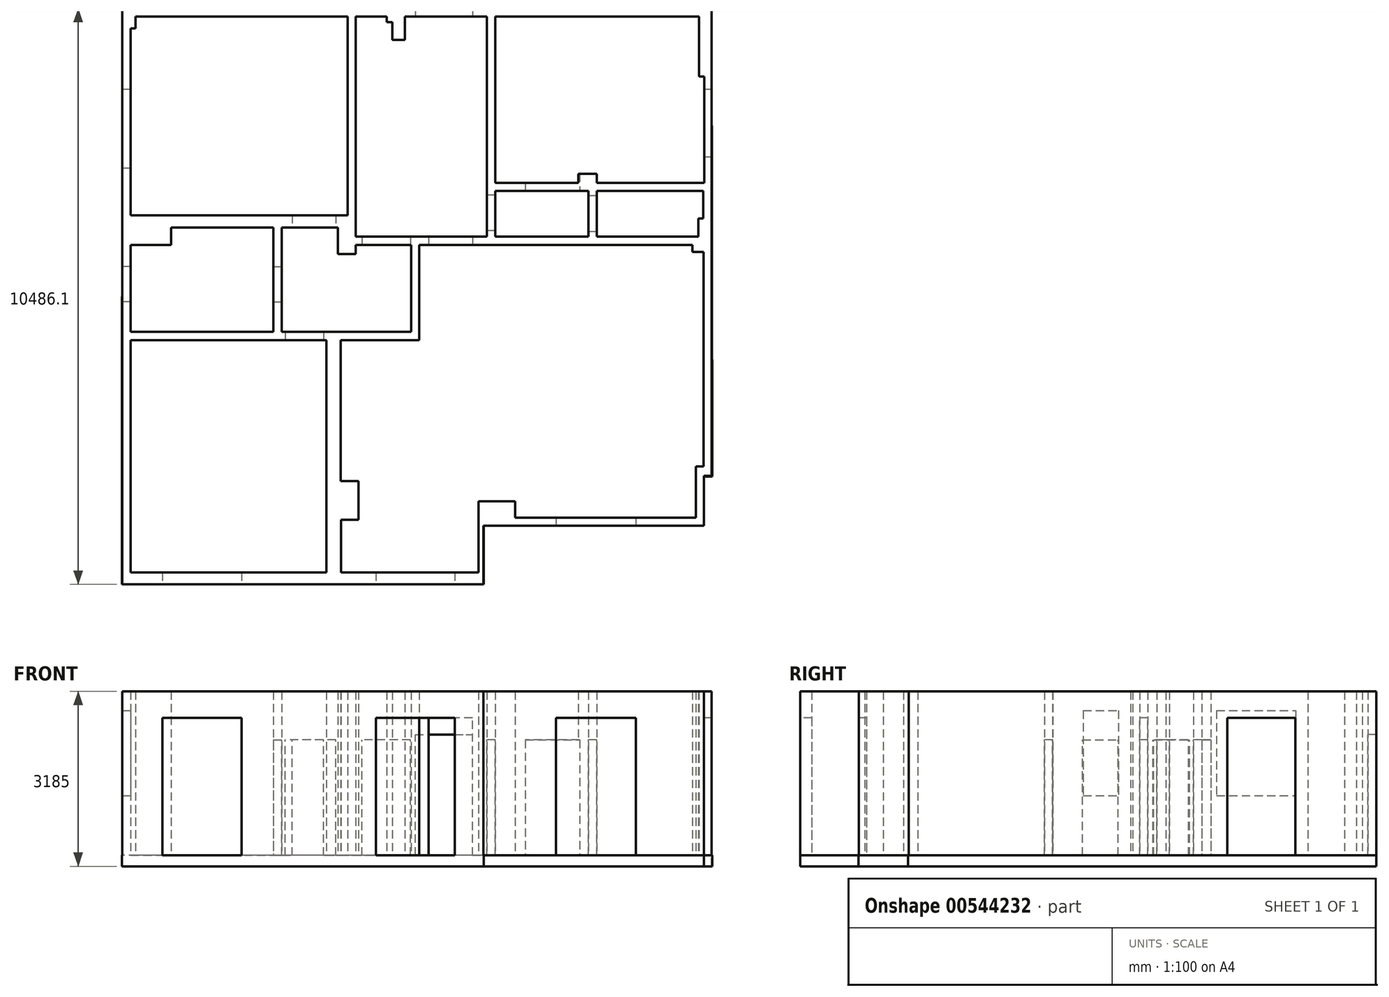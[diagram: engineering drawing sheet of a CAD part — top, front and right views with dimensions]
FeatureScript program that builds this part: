
annotation { "Feature Type Name" : "Feature", "Feature Type Description" : "" }
export const myFeature = defineFeature(function(context is Context, id is Id, definition is map)
    precondition{}
    {
        {
            var Q0;
            Q0=qCreatedBy(makeId("Top.planeOp"),FACE);
            var sketch = newSketch(context, id + "F0", { "sketchPlane" : qUnion([Q0])});
            skLineSegment(sketch, "E0", {"start": v(0, 0) * mm, "end": v(4001, 0) * mm});
            skLineSegment(sketch, "E1", {"start": v(4001, 0) * mm, "end": v(4001, -125) * mm});
            skLineSegment(sketch, "E2", {"start": v(4001, -125) * mm, "end": v(4202.95, -125) * mm});
            skLineSegment(sketch, "E3", {"start": v(4202.95, -125) * mm, "end": v(4202.95, -4036) * mm});
            skLineSegment(sketch, "E4", {"start": v(4202.95, -4036) * mm, "end": v(4062.95, -4036) * mm});
            skLineSegment(sketch, "E5", {"start": v(4062.95, -4036) * mm, "end": v(4062.95, -4967) * mm});
            skLineSegment(sketch, "E6", {"start": v(4062.95, -4967) * mm, "end": v(2970.95, -4967) * mm});
            skLineSegment(sketch, "E7", {"start": v(2970.95, -4967) * mm, "end": v(1520.95, -4967) * mm});
            skLineSegment(sketch, "E8", {"start": v(1520.95, -4967) * mm, "end": v(778.95, -4967) * mm});
            skLineSegment(sketch, "E9", {"start": v(-797, 0) * mm, "end": v(0, 0) * mm});
            skLineSegment(sketch, "E10", {"start": v(778.95, -4967) * mm, "end": v(778.95, -4667) * mm});
            skLineSegment(sketch, "E11", {"start": v(778.95, -4667) * mm, "end": v(106.95, -4667) * mm});
            skLineSegment(sketch, "E12", {"start": v(106.95, -4667) * mm, "end": v(106.95, -5966) * mm});
            skLineSegment(sketch, "E13", {"start": v(106.95, -5966) * mm, "end": v(-320.05, -5966) * mm});
            skLineSegment(sketch, "E14", {"start": v(-320.05, -5966) * mm, "end": v(-1760.05, -5966) * mm});
            skLineSegment(sketch, "E15", {"start": v(-1760.05, -5966) * mm, "end": v(-2394.05, -5966) * mm});
            skLineSegment(sketch, "E16", {"start": v(-2394.05, -5966) * mm, "end": v(-2394.05, -5002) * mm});
            skLineSegment(sketch, "E17", {"start": v(-2394.05, -5002) * mm, "end": v(-2075.05, -5002) * mm});
            skLineSegment(sketch, "E18", {"start": v(-2075.05, -5002) * mm, "end": v(-2075.05, -4297) * mm});
            skLineSegment(sketch, "E19", {"start": v(-2075.05, -4297) * mm, "end": v(-2399.05, -4297) * mm});
            skLineSegment(sketch, "E20", {"start": v(-2399.05, -4297) * mm, "end": v(-2399.05, -1733) * mm});
            skLineSegment(sketch, "E21", {"start": v(-797, 0) * mm, "end": v(-967, 0) * mm});
            skLineSegment(sketch, "E22", {"start": v(-967, 0) * mm, "end": v(-967, -1733) * mm});
            skLineSegment(sketch, "E23", {"start": v(-2399.05, -1733) * mm, "end": v(-967, -1733) * mm});
            skLineSegment(sketch, "E24.1", {"start": v(-797, -5.1) * mm, "end": v(-961.9, -5.1) * mm});
            skLineSegment(sketch, "E24.5", {"start": v(-2181.9, -4291.9) * mm, "end": v(-2505.9, -4291.9) * mm});
            skLineSegment(sketch, "E24.11", {"start": v(-797, -5.1) * mm, "end": v(0, -5.1) * mm});
            skLineSegment(sketch, "E24.19", {"start": v(3945.9, -4961.9) * mm, "end": v(2859, -4961.9) * mm});
            skLineSegment(sketch, "E25.0", {"start": v(0, 150) * mm, "end": v(264.38, 150) * mm});
            skLineSegment(sketch, "E26.0", {"start": v(2800.47, -5111.9) * mm, "end": v(1350.47, -5111.9) * mm});
            skLineSegment(sketch, "E27.0", {"start": v(1409, -5111.9) * mm, "end": v(720.85, -5111.9) * mm});
            skLineSegment(sketch, "E28", {"start": v(720.85, -5111.9) * mm, "end": v(198.85, -5111.9) * mm});
            skLineSegment(sketch, "E29", {"start": v(198.85, -5111.9) * mm, "end": v(198.85, -6179.3) * mm});
            skLineSegment(sketch, "E30", {"start": v(-435.2, -6179.3) * mm, "end": v(198.85, -6179.3) * mm});
            skLineSegment(sketch, "E31", {"start": v(2800.47, -5111.9) * mm, "end": v(4212.95, -5111.9) * mm});
            skLineSegment(sketch, "E32", {"start": v(-435.2, -6179.3) * mm, "end": v(-1872, -6179.3) * mm});
            skLineSegment(sketch, "E33", {"start": v(-1872, -6179.3) * mm, "end": v(-2660.9, -6179.3) * mm});
            skLineSegment(sketch, "E34", {"start": v(-2660.9, -1733) * mm, "end": v(-2660.9, -5966) * mm});
            skLineSegment(sketch, "E35", {"start": v(-2660.9, -1583) * mm, "end": v(-1117, -1583) * mm});
            skLineSegment(sketch, "E36", {"start": v(-1117, 0) * mm, "end": v(-1117, -1583) * mm});
            skLineSegment(sketch, "E37", {"start": v(0, 150) * mm, "end": v(-1117, 150) * mm});
            skPoint(sketch, "E38.orphan", {"position": v(-1117, 0) * mm});
            skLineSegment(sketch, "E39", {"start": v(-1227.62, 4156.8) * mm, "end": v(-1227.62, 3731.8) * mm});
            skLineSegment(sketch, "E40", {"start": v(-1227.62, 3731.8) * mm, "end": v(-1461.62, 3731.8) * mm});
            skLineSegment(sketch, "E41", {"start": v(-1461.62, 3731.8) * mm, "end": v(-1461.62, 4055.8) * mm});
            skLineSegment(sketch, "E42", {"start": v(-1461.62, 4055.8) * mm, "end": v(-1562.62, 4055.8) * mm});
            skLineSegment(sketch, "E43", {"start": v(-1562.62, 4055.8) * mm, "end": v(-1562.62, 4156.8) * mm});
            skLineSegment(sketch, "E44", {"start": v(-1562.62, 4156.8) * mm, "end": v(-2123.62, 4156.8) * mm});
            skLineSegment(sketch, "E45", {"start": v(-2123.62, 4156.8) * mm, "end": v(-2123.62, 150) * mm});
            skLineSegment(sketch, "E46", {"start": v(264.38, 4156.8) * mm, "end": v(264.38, 150) * mm});
            skLineSegment(sketch, "E47", {"start": v(-1227.62, 4156.8) * mm, "end": v(264.38, 4156.8) * mm});
            skLineSegment(sketch, "E48.0", {"start": v(4198.9, 479.37) * mm, "end": v(4198.9, 981.37) * mm});
            skLineSegment(sketch, "E49", {"start": v(4108.9, 479.37) * mm, "end": v(4108.9, 149.4) * mm});
            skLineSegment(sketch, "E50", {"start": v(4108.9, 479.37) * mm, "end": v(4198.9, 479.37) * mm});
            skLineSegment(sketch, "E51", {"start": v(2259.9, 981.37) * mm, "end": v(4198.9, 981.37) * mm});
            skLineSegment(sketch, "E52.0", {"start": v(2262.52, 1131.37) * mm, "end": v(4215.38, 1131.37) * mm});
            skLineSegment(sketch, "E53", {"start": v(2262.52, 1131.37) * mm, "end": v(2262.52, 1296.37) * mm});
            skLineSegment(sketch, "E54", {"start": v(2262.52, 1296.37) * mm, "end": v(1923.52, 1296.37) * mm});
            skLineSegment(sketch, "E55", {"start": v(1923.52, 1296.37) * mm, "end": v(1923.52, 1131.37) * mm});
            skLineSegment(sketch, "E56.0", {"start": v(414.38, 4156.8) * mm, "end": v(414.38, 1131.37) * mm});
            skLineSegment(sketch, "E57", {"start": v(-2273.62, 4306.8) * mm, "end": v(4352.95, 4306.8) * mm});
            skLineSegment(sketch, "E58", {"start": v(414.38, 4156.8) * mm, "end": v(4125.38, 4156.8) * mm});
            skLineSegment(sketch, "E59.trimOffspring", {"start": v(4125.38, 4156.8) * mm, "end": v(4125.38, 3063.8) * mm});
            skLineSegment(sketch, "E60", {"start": v(1923.52, 1131.37) * mm, "end": v(414.38, 1131.37) * mm});
            skLineSegment(sketch, "E61", {"start": v(2259.9, 981.37) * mm, "end": v(2259.9, 149.78) * mm});
            skLineSegment(sketch, "E62", {"start": v(2259.9, 149.78) * mm, "end": v(4108.9, 149.4) * mm});
            skLineSegment(sketch, "E63.0", {"start": v(2109.9, 981.37) * mm, "end": v(2109.9, 149.67) * mm});
            skLineSegment(sketch, "E64", {"start": v(2109.9, 981.37) * mm, "end": v(414.38, 981.37) * mm});
            skLineSegment(sketch, "E65.trimOffspring", {"start": v(414.38, 981.37) * mm, "end": v(414.38, 150) * mm});
            skLineSegment(sketch, "E66", {"start": v(-2273.62, 4156.8) * mm, "end": v(-2273.62, 541.1) * mm});
            skLineSegment(sketch, "E67.trimOffspring", {"start": v(414.38, 150) * mm, "end": v(2109.9, 150) * mm});
            skLineSegment(sketch, "E68", {"start": v(-1117, 150) * mm, "end": v(-2123.62, 150) * mm});
            skLineSegment(sketch, "E69.trimOffspring", {"start": v(2259.9, 150) * mm, "end": v(4001, 150) * mm});
            skLineSegment(sketch, "E70", {"start": v(-2123.62, 0) * mm, "end": v(-2123.62, -166) * mm});
            skLineSegment(sketch, "E71", {"start": v(-2123.62, -166) * mm, "end": v(-2448.62, -166) * mm});
            skLineSegment(sketch, "E72", {"start": v(-2448.62, -166) * mm, "end": v(-2448.62, 316) * mm});
            skLineSegment(sketch, "E73", {"start": v(-3472.9, 316) * mm, "end": v(-3472.9, -1579.32) * mm});
            skLineSegment(sketch, "E74", {"start": v(-2448.62, 316) * mm, "end": v(-3472.9, 316) * mm});
            skLineSegment(sketch, "E75", {"start": v(-3472.9, -1579.32) * mm, "end": v(-2660.9, -1583) * mm});
            skLineSegment(sketch, "E76", {"start": v(-3622.9, 541.1) * mm, "end": v(-2273.62, 541.1) * mm});
            skLineSegment(sketch, "E77", {"start": v(-3622.9, 316) * mm, "end": v(-3622.9, -1583) * mm});
            skLineSegment(sketch, "E78", {"start": v(-1117, 0) * mm, "end": v(-2123.62, 0) * mm});
            skLineSegment(sketch, "E79", {"start": v(-2660.9, -1733) * mm, "end": v(-6222.9, -1733) * mm});
            skLineSegment(sketch, "E80", {"start": v(-6222.9, -1733) * mm, "end": v(-6222.9, -5966) * mm});
            skLineSegment(sketch, "E81", {"start": v(-2660.9, -5966) * mm, "end": v(-6222.9, -5966) * mm});
            skLineSegment(sketch, "E82", {"start": v(-2660.9, -6179.3) * mm, "end": v(-6372.9, -6179.3) * mm});
            skLineSegment(sketch, "E83", {"start": v(-6372.9, 541.1) * mm, "end": v(-6372.9, -6179.3) * mm});
            skLineSegment(sketch, "E84", {"start": v(-3622.9, -1583) * mm, "end": v(-6222.9, -1583) * mm});
            skLineSegment(sketch, "E85", {"start": v(-6222.9, -1583) * mm, "end": v(-6222.9, 0) * mm});
            skLineSegment(sketch, "E86", {"start": v(-3622.9, 316) * mm, "end": v(-5487.9, 316) * mm});
            skLineSegment(sketch, "E87", {"start": v(-5487.9, 316) * mm, "end": v(-5487.9, 0) * mm});
            skLineSegment(sketch, "E88", {"start": v(-6222.9, 0) * mm, "end": v(-5487.9, 0) * mm});
            skLineSegment(sketch, "E89", {"start": v(-3622.9, 541.1) * mm, "end": v(-6222.9, 541.1) * mm});
            skLineSegment(sketch, "E90", {"start": v(-6372.9, 541.1) * mm, "end": v(-6372.9, 4306.8) * mm});
            skLineSegment(sketch, "E91", {"start": v(-2273.62, 4306.8) * mm, "end": v(-6372.9, 4306.8) * mm});
            skLineSegment(sketch, "E92", {"start": v(-6222.9, 541.1) * mm, "end": v(-6222.9, 3944.8) * mm});
            skLineSegment(sketch, "E93", {"start": v(-2273.62, 4156.8) * mm, "end": v(-6132.9, 4156.8) * mm});
            skLineSegment(sketch, "E94", {"start": v(-6132.9, 4156.8) * mm, "end": v(-6132.9, 3944.8) * mm});
            skLineSegment(sketch, "E95.trimOffspring", {"start": v(-6222.9, 3944.8) * mm, "end": v(-6132.9, 3944.8) * mm});
            skLineSegment(sketch, "E96", {"start": v(4125.38, 3063.8) * mm, "end": v(4215.38, 3063.8) * mm});
            skLineSegment(sketch, "E97", {"start": v(4215.38, 3063.8) * mm, "end": v(4215.38, 1131.37) * mm});
            skLineSegment(sketch, "E98", {"start": v(4352.95, 4306.8) * mm, "end": v(4352.95, -4204.43) * mm});
            skLineSegment(sketch, "E99", {"start": v(4212.95, -4204.43) * mm, "end": v(4212.95, -5111.9) * mm});
            skLineSegment(sketch, "E100.trimOffspring", {"start": v(4212.95, -4204.43) * mm, "end": v(4352.95, -4204.43) * mm});
            skSolve(sketch);
        }
        {
            var Q0;
            Q0 = qSketchRegion(id + "F0", true);
            extrude(context, id + "F1", {"entities" : qUnion([Q0]), "depth" : 2985 * mm, "offsetDistance" : 25 * mm});
        }
        {
            var Q0;
            Q0=makeQuery(id+"F1.opExtrude","SWEPT_FACE",FACE,{"disambiguationData":[OSD([sQuery(id+"F0.wireOp",EDGE,"E26.0"),sQuery(id+"F0.wireOp",EDGE,"E27.0"),sQuery(id+"F0.wireOp",EDGE,"E28"),sQuery(id+"F0.wireOp",EDGE,"E31")])]});
            var sketch = newSketch(context, id + "F2", { "sketchPlane" : qUnion([Q0])});
            skLineSegment(sketch, "E101.bottom", {"start": v(2970.95, 0) * mm, "end": v(1520.95, 0) * mm});
            skLineSegment(sketch, "E101.top", {"start": v(2970.95, 2500) * mm, "end": v(1520.95, 2500) * mm});
            skLineSegment(sketch, "E101.left", {"start": v(2970.95, 0) * mm, "end": v(2970.95, 2500) * mm});
            skLineSegment(sketch, "E101.right", {"start": v(1520.95, 0) * mm, "end": v(1520.95, 2500) * mm});
            skSolve(sketch);
        }
        {
            var Q0;
            Q0 = qSketchRegion(id + "F2", true);
            extrude(context, id + "F3", {"entities" : qUnion([Q0]), "operationType" : NewBodyOperationType.REMOVE, "endBound" : BoundingType.UP_TO_NEXT, "oppositeDirection" : true, "depth" : 25 * mm, "offsetDistance" : 25 * mm});
        }
        {
            var Q0;
            Q0=makeQuery(id+"F1.opExtrude","SWEPT_FACE",FACE,{"disambiguationData":[OSD([sQuery(id+"F0.wireOp",EDGE,"E30"),sQuery(id+"F0.wireOp",EDGE,"E32"),sQuery(id+"F0.wireOp",EDGE,"E33"),sQuery(id+"F0.wireOp",EDGE,"E82")])]});
            var sketch = newSketch(context, id + "F4", { "sketchPlane" : qUnion([Q0])});
            skLineSegment(sketch, "E102.bottom", {"start": v(-320.05, 0) * mm, "end": v(-1760.05, 0) * mm});
            skLineSegment(sketch, "E102.top", {"start": v(-320.05, 2500) * mm, "end": v(-1760.05, 2500) * mm});
            skLineSegment(sketch, "E102.left", {"start": v(-320.05, 0) * mm, "end": v(-320.05, 2500) * mm});
            skLineSegment(sketch, "E102.right", {"start": v(-1760.05, 0) * mm, "end": v(-1760.05, 2500) * mm});
            skSolve(sketch);
        }
        {
            var Q0;
            Q0 = qSketchRegion(id + "F4", true);
            extrude(context, id + "F5", {"entities" : qUnion([Q0]), "operationType" : NewBodyOperationType.REMOVE, "endBound" : BoundingType.UP_TO_NEXT, "oppositeDirection" : true, "depth" : 25 * mm, "offsetDistance" : 25 * mm});
        }
        {
            var Q0;
            Q0=makeQuery(id+"F1.opExtrude","SWEPT_FACE",FACE,{"disambiguationData":[OSD([sQuery(id+"F0.wireOp",EDGE,"E30"),sQuery(id+"F0.wireOp",EDGE,"E32"),sQuery(id+"F0.wireOp",EDGE,"E33"),sQuery(id+"F0.wireOp",EDGE,"E82")])]});
            var sketch = newSketch(context, id + "F6", { "sketchPlane" : qUnion([Q0])});
            skLineSegment(sketch, "E103.bottom", {"start": v(-4201.9, 0) * mm, "end": v(-5644.9, 0) * mm});
            skLineSegment(sketch, "E103.top", {"start": v(-4201.9, 2500) * mm, "end": v(-5644.9, 2500) * mm});
            skLineSegment(sketch, "E103.left", {"start": v(-4201.9, 0) * mm, "end": v(-4201.9, 2500) * mm});
            skLineSegment(sketch, "E103.right", {"start": v(-5644.9, 0) * mm, "end": v(-5644.9, 2500) * mm});
            skSolve(sketch);
        }
        {
            var Q0;
            Q0 = qSketchRegion(id + "F6", true);
            extrude(context, id + "F7", {"entities" : qUnion([Q0]), "operationType" : NewBodyOperationType.REMOVE, "endBound" : BoundingType.UP_TO_NEXT, "oppositeDirection" : true, "depth" : 25 * mm, "offsetDistance" : 25 * mm});
        }
        {
            var Q0;
            Q0=makeQuery(id+"F1.opExtrude","SWEPT_FACE",FACE,{"disambiguationData":[OSD([sQuery(id+"F0.wireOp",EDGE,"E0"),sQuery(id+"F0.wireOp",EDGE,"E9"),sQuery(id+"F0.wireOp",EDGE,"E21")])]});
            var sketch = newSketch(context, id + "F8", { "sketchPlane" : qUnion([Q0])});
            skLineSegment(sketch, "E104.bottom", {"start": v(0, 0) * mm, "end": v(-797, 0) * mm});
            skLineSegment(sketch, "E104.top", {"start": v(0, 2500) * mm, "end": v(-797, 2500) * mm});
            skLineSegment(sketch, "E104.left", {"start": v(0, 0) * mm, "end": v(0, 2500) * mm});
            skLineSegment(sketch, "E104.right", {"start": v(-797, 0) * mm, "end": v(-797, 2500) * mm});
            skSolve(sketch);
        }
        {
            var Q0;
            Q0 = qSketchRegion(id + "F8", true);
            extrude(context, id + "F9", {"entities" : qUnion([Q0]), "operationType" : NewBodyOperationType.REMOVE, "endBound" : BoundingType.UP_TO_NEXT, "oppositeDirection" : true, "depth" : 25 * mm, "offsetDistance" : 25 * mm});
        }
        {
            var Q0;
            Q0=makeQuery(id+"F1.opExtrude","SWEPT_FACE",FACE,{"disambiguationData":[OSD([sQuery(id+"F0.wireOp",EDGE,"E64")])]});
            var sketch = newSketch(context, id + "F10", { "sketchPlane" : qUnion([Q0])});
            skLineSegment(sketch, "E105.bottom", {"start": v(1951.38, 0) * mm, "end": v(962.38, 0) * mm});
            skLineSegment(sketch, "E105.top", {"start": v(1951.38, 2100) * mm, "end": v(962.38, 2100) * mm});
            skLineSegment(sketch, "E105.left", {"start": v(1951.38, 0) * mm, "end": v(1951.38, 2100) * mm});
            skLineSegment(sketch, "E105.right", {"start": v(962.38, 0) * mm, "end": v(962.38, 2100) * mm});
            skSolve(sketch);
        }
        {
            var Q0;
            Q0 = qSketchRegion(id + "F10", true);
            extrude(context, id + "F11", {"entities" : qUnion([Q0]), "operationType" : NewBodyOperationType.REMOVE, "endBound" : BoundingType.UP_TO_NEXT, "oppositeDirection" : true, "depth" : 25 * mm, "offsetDistance" : 25 * mm});
        }
        {
            var Q0;
            Q0=makeQuery(id+"F1.opExtrude","SWEPT_FACE",FACE,{"disambiguationData":[OSD([sQuery(id+"F0.wireOp",EDGE,"E46")])]});
            var sketch = newSketch(context, id + "F12", { "sketchPlane" : qUnion([Q0])});
            skLineSegment(sketch, "E106.bottom", {"start": v(-258.95, 0) * mm, "end": v(-906.95, 0) * mm});
            skLineSegment(sketch, "E106.top", {"start": v(-258.95, 2100) * mm, "end": v(-906.95, 2100) * mm});
            skLineSegment(sketch, "E106.left", {"start": v(-258.95, 0) * mm, "end": v(-258.95, 2100) * mm});
            skLineSegment(sketch, "E106.right", {"start": v(-906.95, 0) * mm, "end": v(-906.95, 2100) * mm});
            skSolve(sketch);
        }
        {
            var Q0;
            Q0 = qSketchRegion(id + "F12", true);
            extrude(context, id + "F13", {"entities" : qUnion([Q0]), "operationType" : NewBodyOperationType.REMOVE, "endBound" : BoundingType.UP_TO_NEXT, "oppositeDirection" : true, "depth" : 25 * mm, "offsetDistance" : 25 * mm});
        }
        {
            var Q0;
            Q0=makeQuery(id+"F1.opExtrude","SWEPT_FACE",FACE,{"disambiguationData":[OSD([sQuery(id+"F0.wireOp",EDGE,"E63.0")])]});
            var sketch = newSketch(context, id + "F14", { "sketchPlane" : qUnion([Q0])});
            skLineSegment(sketch, "E107.bottom", {"start": v(-891.37, 0) * mm, "end": v(-243.37, 0) * mm});
            skLineSegment(sketch, "E107.top", {"start": v(-891.37, 2100) * mm, "end": v(-243.37, 2100) * mm});
            skLineSegment(sketch, "E107.left", {"start": v(-891.37, 0) * mm, "end": v(-891.37, 2100) * mm});
            skLineSegment(sketch, "E107.right", {"start": v(-243.37, 0) * mm, "end": v(-243.37, 2100) * mm});
            skSolve(sketch);
        }
        {
            var Q0;
            Q0 = qSketchRegion(id + "F14", true);
            extrude(context, id + "F15", {"entities" : qUnion([Q0]), "operationType" : NewBodyOperationType.REMOVE, "endBound" : BoundingType.UP_TO_NEXT, "oppositeDirection" : true, "depth" : 25 * mm, "offsetDistance" : 25 * mm});
        }
        {
            var Q0;
            Q0=makeQuery(id+"F1.opExtrude","SWEPT_FACE",FACE,{"disambiguationData":[OSD([sQuery(id+"F0.wireOp",EDGE,"E47")])]});
            var sketch = newSketch(context, id + "F16", { "sketchPlane" : qUnion([Q0])});
            skLineSegment(sketch, "E108.bottom", {"start": v(-1042, 0) * mm, "end": v(0, 0) * mm});
            skLineSegment(sketch, "E108.top", {"start": v(-1042, 2200) * mm, "end": v(0, 2200) * mm});
            skLineSegment(sketch, "E108.left", {"start": v(-1042, 0) * mm, "end": v(-1042, 2200) * mm});
            skLineSegment(sketch, "E108.right", {"start": v(0, 0) * mm, "end": v(0, 2200) * mm});
            skSolve(sketch);
        }
        {
            var Q0;
            Q0 = qSketchRegion(id + "F16", true);
            extrude(context, id + "F17", {"entities" : qUnion([Q0]), "operationType" : NewBodyOperationType.REMOVE, "endBound" : BoundingType.UP_TO_NEXT, "oppositeDirection" : true, "depth" : 25 * mm, "offsetDistance" : 25 * mm});
        }
        {
            var Q0;
            Q0=makeQuery(id+"F1.opExtrude","SWEPT_FACE",FACE,{"disambiguationData":[OSD([sQuery(id+"F0.wireOp",EDGE,"E97")])]});
            var sketch = newSketch(context, id + "F18", { "sketchPlane" : qUnion([Q0])});
            skLineSegment(sketch, "E109.bottom", {"start": v(-2833.8, 0) * mm, "end": v(-1598.8, 0) * mm});
            skLineSegment(sketch, "E109.top", {"start": v(-2833.8, 2500) * mm, "end": v(-1598.8, 2500) * mm});
            skLineSegment(sketch, "E109.left", {"start": v(-2833.8, 0) * mm, "end": v(-2833.8, 2500) * mm});
            skLineSegment(sketch, "E109.right", {"start": v(-1598.8, 0) * mm, "end": v(-1598.8, 2500) * mm});
            skSolve(sketch);
        }
        {
            var Q0;
            Q0 = qSketchRegion(id + "F18", true);
            extrude(context, id + "F19", {"entities" : qUnion([Q0]), "operationType" : NewBodyOperationType.REMOVE, "endBound" : BoundingType.UP_TO_NEXT, "oppositeDirection" : true, "depth" : 25 * mm, "offsetDistance" : 25 * mm});
        }
        {
            var Q0;
            Q0=makeQuery(id+"F1.opExtrude","SWEPT_FACE",FACE,{"disambiguationData":[OSD([sQuery(id+"F0.wireOp",EDGE,"E79")])]});
            var sketch = newSketch(context, id + "F20", { "sketchPlane" : qUnion([Q0])});
            skLineSegment(sketch, "E110.bottom", {"start": v(-2710.9, 0) * mm, "end": v(-3410.9, 0) * mm});
            skLineSegment(sketch, "E110.top", {"start": v(-2710.9, 2100) * mm, "end": v(-3410.9, 2100) * mm});
            skLineSegment(sketch, "E110.left", {"start": v(-2710.9, 0) * mm, "end": v(-2710.9, 2100) * mm});
            skLineSegment(sketch, "E110.right", {"start": v(-3410.9, 0) * mm, "end": v(-3410.9, 2100) * mm});
            skSolve(sketch);
        }
        {
            var Q0;
            Q0 = qSketchRegion(id + "F20", true);
            extrude(context, id + "F21", {"entities" : qUnion([Q0]), "operationType" : NewBodyOperationType.REMOVE, "endBound" : BoundingType.UP_TO_NEXT, "oppositeDirection" : true, "depth" : 25 * mm, "offsetDistance" : 25 * mm});
        }
        {
            var Q0;
            Q0=makeQuery(id+"F1.opExtrude","SWEPT_FACE",FACE,{"disambiguationData":[OSD([sQuery(id+"F0.wireOp",EDGE,"E74")])]});
            var sketch = newSketch(context, id + "F22", { "sketchPlane" : qUnion([Q0])});
            skLineSegment(sketch, "E111.bottom", {"start": v(-2488.9, 0) * mm, "end": v(-3282.9, 0) * mm});
            skLineSegment(sketch, "E111.top", {"start": v(-2488.9, 2100) * mm, "end": v(-3282.9, 2100) * mm});
            skLineSegment(sketch, "E111.left", {"start": v(-2488.9, 0) * mm, "end": v(-2488.9, 2100) * mm});
            skLineSegment(sketch, "E111.right", {"start": v(-3282.9, 0) * mm, "end": v(-3282.9, 2100) * mm});
            skSolve(sketch);
        }
        {
            var Q0;
            Q0 = qSketchRegion(id + "F22", true);
            extrude(context, id + "F23", {"entities" : qUnion([Q0]), "operationType" : NewBodyOperationType.REMOVE, "endBound" : BoundingType.UP_TO_NEXT, "oppositeDirection" : true, "depth" : 25 * mm, "offsetDistance" : 25 * mm});
        }
        {
            var Q0;
            Q0=makeQuery(id+"F1.opExtrude","SWEPT_FACE",FACE,{"disambiguationData":[OSD([sQuery(id+"F0.wireOp",EDGE,"E78")])]});
            var sketch = newSketch(context, id + "F24", { "sketchPlane" : qUnion([Q0])});
            skLineSegment(sketch, "E112.bottom", {"start": v(-1129.62, 0) * mm, "end": v(-2013.62, 0) * mm});
            skLineSegment(sketch, "E112.top", {"start": v(-1129.62, 2100) * mm, "end": v(-2013.62, 2100) * mm});
            skLineSegment(sketch, "E112.left", {"start": v(-1129.62, 0) * mm, "end": v(-1129.62, 2100) * mm});
            skLineSegment(sketch, "E112.right", {"start": v(-2013.62, 0) * mm, "end": v(-2013.62, 2100) * mm});
            skSolve(sketch);
        }
        {
            var Q0;
            Q0 = qSketchRegion(id + "F24", true);
            extrude(context, id + "F25", {"entities" : qUnion([Q0]), "operationType" : NewBodyOperationType.REMOVE, "endBound" : BoundingType.UP_TO_NEXT, "oppositeDirection" : true, "depth" : 25 * mm, "offsetDistance" : 25 * mm});
        }
        {
            var Q0;
            Q0=makeQuery(id+"F1.opExtrude","SWEPT_FACE",FACE,{"disambiguationData":[OSD([sQuery(id+"F0.wireOp",EDGE,"E73")])]});
            var sketch = newSketch(context, id + "F26", { "sketchPlane" : qUnion([Q0])});
            skLineSegment(sketch, "E113.bottom", {"start": v(-1039, 0) * mm, "end": v(-393, 0) * mm});
            skLineSegment(sketch, "E113.top", {"start": v(-1039, 2100) * mm, "end": v(-393, 2100) * mm});
            skLineSegment(sketch, "E113.left", {"start": v(-1039, 0) * mm, "end": v(-1039, 2100) * mm});
            skLineSegment(sketch, "E113.right", {"start": v(-393, 0) * mm, "end": v(-393, 2100) * mm});
            skSolve(sketch);
        }
        {
            var Q0;
            Q0 = qSketchRegion(id + "F26", true);
            extrude(context, id + "F27", {"entities" : qUnion([Q0]), "operationType" : NewBodyOperationType.REMOVE, "endBound" : BoundingType.UP_TO_NEXT, "oppositeDirection" : true, "depth" : 25 * mm, "offsetDistance" : 25 * mm});
        }
        {
            var Q0;
            Q0=makeQuery(id+"F1.opExtrude","SWEPT_FACE",FACE,{"disambiguationData":[OSD([sQuery(id+"F0.wireOp",EDGE,"E85")])]});
            var sketch = newSketch(context, id + "F28", { "sketchPlane" : qUnion([Q0])});
            skLineSegment(sketch, "E114.bottom", {"start": v(-1027.15, 2635) * mm, "end": v(-387.15, 2635) * mm});
            skLineSegment(sketch, "E114.top", {"start": v(-1027.15, 1085) * mm, "end": v(-387.15, 1085) * mm});
            skLineSegment(sketch, "E114.left", {"start": v(-1027.15, 2635) * mm, "end": v(-1027.15, 1085) * mm});
            skLineSegment(sketch, "E114.right", {"start": v(-387.15, 2635) * mm, "end": v(-387.15, 1085) * mm});
            skSolve(sketch);
        }
        {
            var Q0;
            Q0 = qSketchRegion(id + "F28", true);
            extrude(context, id + "F29", {"entities" : qUnion([Q0]), "operationType" : NewBodyOperationType.REMOVE, "endBound" : BoundingType.UP_TO_NEXT, "oppositeDirection" : true, "depth" : 25 * mm, "offsetDistance" : 25 * mm});
        }
        {
            var Q0;
            Q0=makeQuery(id+"F1.opExtrude","SWEPT_FACE",FACE,{"disambiguationData":[OSD([sQuery(id+"F0.wireOp",EDGE,"E92")])]});
            var sketch = newSketch(context, id + "F30", { "sketchPlane" : qUnion([Q0])});
            skLineSegment(sketch, "E115.bottom", {"start": v(1400.8, 2635) * mm, "end": v(2838.8, 2635) * mm});
            skLineSegment(sketch, "E115.top", {"start": v(1400.8, 1085) * mm, "end": v(2838.8, 1085) * mm});
            skLineSegment(sketch, "E115.left", {"start": v(1400.8, 2635) * mm, "end": v(1400.8, 1085) * mm});
            skLineSegment(sketch, "E115.right", {"start": v(2838.8, 2635) * mm, "end": v(2838.8, 1085) * mm});
            skSolve(sketch);
        }
        {
            var Q0;
            Q0 = qSketchRegion(id + "F30", true);
            extrude(context, id + "F31", {"entities" : qUnion([Q0]), "operationType" : NewBodyOperationType.REMOVE, "endBound" : BoundingType.UP_TO_NEXT, "oppositeDirection" : true, "depth" : 25 * mm, "offsetDistance" : 25 * mm});
        }
        {
            var Q0;
            {var subQ1=sQuery(id+"F0.wireOp",EDGE,"E36");var subQ5=sQuery(id+"F0.wireOp",EDGE,"E17");var subQ7=sQuery(id+"F0.wireOp",EDGE,"E75");var subQ9=sQuery(id+"F0.wireOp",EDGE,"E81");var subQ11=sQuery(id+"F0.wireOp",EDGE,"E68");var subQ12=sQuery(id+"F0.wireOp",EDGE,"E37");var subQ13=sQuery(id+"F0.wireOp",EDGE,"E25.0");var subQ15=sQuery(id+"F0.wireOp",EDGE,"E34");var subQ17=sQuery(id+"F0.wireOp",EDGE,"E82");var subQ18=sQuery(id+"F0.wireOp",EDGE,"E33");var subQ19=sQuery(id+"F0.wireOp",EDGE,"E32");var subQ20=sQuery(id+"F0.wireOp",EDGE,"E30");var subQ22=sQuery(id+"F0.wireOp",EDGE,"E16");var subQ23=makeQuery(id+"F1.opExtrude","SWEPT_FACE",FACE,{"disambiguationData":[OSD([subQ22])]});var subQ24=sQuery(id+"F0.wireOp",EDGE,"E35");var subQ26=sQuery(id+"F0.wireOp",EDGE,"E21");var subQ27=sQuery(id+"F0.wireOp",EDGE,"E9");var subQ28=sQuery(id+"F0.wireOp",EDGE,"E0");var subQ30=sQuery(id+"F0.wireOp",EDGE,"E15");var subQ31=sQuery(id+"F0.wireOp",EDGE,"E14");var subQ32=sQuery(id+"F0.wireOp",EDGE,"E13");var subQ34=sQuery(id+"F0.wireOp",EDGE,"E18");var subQ36=sQuery(id+"F0.wireOp",EDGE,"E19");var subQ39=sQuery(id+"F0.wireOp",EDGE,"E23");var subQ41=sQuery(id+"F0.wireOp",EDGE,"E20");var subQ43=sQuery(id+"F0.wireOp",EDGE,"E78");var subQ45=sQuery(id+"F0.wireOp",EDGE,"E22");var subQ47=sQuery(id+"F0.wireOp",EDGE,"E79");var subQ49=sQuery(id+"F0.wireOp",EDGE,"E84");var subQ51=sQuery(id+"F0.wireOp",EDGE,"E90");var subQ52=sQuery(id+"F0.wireOp",EDGE,"E83");var subQ54=sQuery(id+"F0.wireOp",EDGE,"E72");var subQ56=sQuery(id+"F0.wireOp",EDGE,"E71");var subQ58=sQuery(id+"F0.wireOp",EDGE,"E70");var subQ60=sQuery(id+"F0.wireOp",EDGE,"E66");var subQ62=sQuery(id+"F0.wireOp",EDGE,"E91");var subQ63=sQuery(id+"F0.wireOp",EDGE,"E57");var subQ65=sQuery(id+"F0.wireOp",EDGE,"E80");var subQ67=sQuery(id+"F0.wireOp",EDGE,"E77");var subQ69=sQuery(id+"F0.wireOp",EDGE,"E89");var subQ70=sQuery(id+"F0.wireOp",EDGE,"E76");var subQ72=sQuery(id+"F0.wireOp",EDGE,"E73");var subQ74=sQuery(id+"F0.wireOp",EDGE,"E47");var subQ76=sQuery(id+"F0.wireOp",EDGE,"E87");var subQ78=sQuery(id+"F0.wireOp",EDGE,"E74");var subQ80=sQuery(id+"F0.wireOp",EDGE,"E85");var subQ82=sQuery(id+"F0.wireOp",EDGE,"E86");var subQ84=sQuery(id+"F0.wireOp",EDGE,"E88");var subQ86=sQuery(id+"F0.wireOp",EDGE,"E92");var subQ88=sQuery(id+"F0.wireOp",EDGE,"E39");var subQ90=sQuery(id+"F0.wireOp",EDGE,"E93");var subQ92=sQuery(id+"F0.wireOp",EDGE,"E40");var subQ94=sQuery(id+"F0.wireOp",EDGE,"E94");var subQ96=sQuery(id+"F0.wireOp",EDGE,"E41");var subQ98=sQuery(id+"F0.wireOp",EDGE,"E95.trimOffspring");var subQ100=sQuery(id+"F0.wireOp",EDGE,"E42");var subQ102=sQuery(id+"F0.wireOp",EDGE,"E43");var subQ104=sQuery(id+"F0.wireOp",EDGE,"E44");var subQ106=sQuery(id+"F0.wireOp",EDGE,"E45");var subQ108=sQuery(id+"F0.wireOp",EDGE,"E60");var subQ109=sQuery(id+"F0.wireOp",EDGE,"E59.trimOffspring");var subQ110=sQuery(id+"F0.wireOp",EDGE,"E58");var subQ111=sQuery(id+"F0.wireOp",EDGE,"E56.0");var subQ112=sQuery(id+"F0.wireOp",EDGE,"E55");var subQ113=sQuery(id+"F0.wireOp",EDGE,"E54");var subQ114=sQuery(id+"F0.wireOp",EDGE,"E53");var subQ115=sQuery(id+"F0.wireOp",EDGE,"E52.0");var subQ116=sQuery(id+"F0.wireOp",EDGE,"E51");var subQ117=sQuery(id+"F0.wireOp",EDGE,"E50");var subQ118=sQuery(id+"F0.wireOp",EDGE,"E49");var subQ119=sQuery(id+"F0.wireOp",EDGE,"E48.0");var subQ120=sQuery(id+"F0.wireOp",EDGE,"E46");var subQ121=sQuery(id+"F0.wireOp",EDGE,"E8");var subQ122=sQuery(id+"F0.wireOp",EDGE,"E7");var subQ123=sQuery(id+"F0.wireOp",EDGE,"E6");var subQ124=sQuery(id+"F0.wireOp",EDGE,"E5");var subQ125=sQuery(id+"F0.wireOp",EDGE,"E4");var subQ126=sQuery(id+"F0.wireOp",EDGE,"E61");var subQ127=sQuery(id+"F0.wireOp",EDGE,"E62");var subQ128=sQuery(id+"F0.wireOp",EDGE,"E1");var subQ129=sQuery(id+"F0.wireOp",EDGE,"E63.0");var subQ130=sQuery(id+"F0.wireOp",EDGE,"E2");var subQ131=sQuery(id+"F0.wireOp",EDGE,"E3");var subQ132=sQuery(id+"F0.wireOp",EDGE,"E31");var subQ133=sQuery(id+"F0.wireOp",EDGE,"E28");var subQ134=sQuery(id+"F0.wireOp",EDGE,"E27.0");var subQ135=sQuery(id+"F0.wireOp",EDGE,"E26.0");var subQ136=sQuery(id+"F0.wireOp",EDGE,"E64");var subQ137=sQuery(id+"F0.wireOp",EDGE,"E65.trimOffspring");var subQ138=sQuery(id+"F0.wireOp",EDGE,"E67.trimOffspring");var subQ139=sQuery(id+"F0.wireOp",EDGE,"E96");var subQ140=sQuery(id+"F0.wireOp",EDGE,"E97");var subQ141=sQuery(id+"F0.wireOp",EDGE,"E98");var subQ142=sQuery(id+"F0.wireOp",EDGE,"E99");var subQ143=sQuery(id+"F0.wireOp",EDGE,"E100.trimOffspring");Q0=makeQuery(id+"F25.boolean.opBoolean","SPLIT",FACE,{"disambiguationData":[TD([subQ23])],"derivedFrom":makeQuery(id+"F17.boolean.opBoolean","SPLIT",FACE,{"disambiguationData":[TD([subQ23])],"derivedFrom":makeQuery(id+"F5.boolean.opBoolean","SPLIT",FACE,{"disambiguationData":[TD([makeQuery(id+"F1.opExtrude","SWEPT_FACE",FACE,{"disambiguationData":[OSD([subQ128])]})])],"derivedFrom":makeQuery(id+"F1.opExtrude","CAP_FACE",FACE,{"disambiguationData":[OSD([subQ28,subQ128,subQ130,subQ131,subQ125,subQ124,subQ123,subQ122,subQ121,subQ27,sQuery(id+"F0.wireOp",EDGE,"E10"),sQuery(id+"F0.wireOp",EDGE,"E11"),sQuery(id+"F0.wireOp",EDGE,"E12"),subQ32,subQ31,subQ30,subQ22,subQ5,subQ34,subQ36,subQ41,subQ26,subQ45,subQ39,subQ13,subQ135,subQ134,subQ133,sQuery(id+"F0.wireOp",EDGE,"E29"),subQ20,subQ132,subQ19,subQ18,subQ15,subQ24,subQ1,subQ12,subQ88,subQ92,subQ96,subQ100,subQ102,subQ104,subQ106,subQ120,subQ74,subQ119,subQ118,subQ117,subQ116,subQ115,subQ114,subQ113,subQ112,subQ111,subQ63,subQ110,subQ109,subQ108,subQ126,subQ127,subQ129,subQ136,subQ137,subQ60,subQ138,subQ11,subQ58,subQ56,subQ54,subQ72,subQ78,subQ7,subQ70,subQ67,subQ43,subQ47,subQ65,subQ9,subQ17,subQ52,subQ49,subQ80,subQ82,subQ76,subQ84,subQ69,subQ51,subQ62,subQ86,subQ90,subQ94,subQ98,subQ139,subQ140,subQ141,subQ142,subQ143])],"isStart":true})})})});}
            var sketch = newSketch(context, id + "F32", { "sketchPlane" : qUnion([Q0])});
            skLineSegment(sketch, "E116", {"start": v(-6377.03, 6179.3) * mm, "end": v(202.74, 6179.3) * mm});
            skLineSegment(sketch, "E117", {"start": v(202.74, 6179.3) * mm, "end": v(202.74, 5115.2) * mm});
            skLineSegment(sketch, "E118", {"start": v(202.74, 5115.2) * mm, "end": v(4213.98, 5115.2) * mm});
            skLineSegment(sketch, "E119", {"start": v(4213.98, 5115.2) * mm, "end": v(4213.98, 4216.05) * mm});
            skLineSegment(sketch, "E120", {"start": v(4213.98, 4216.05) * mm, "end": v(4361.62, 4216.05) * mm});
            skLineSegment(sketch, "E121", {"start": v(4361.62, 4216.05) * mm, "end": v(4353.72, -4305.73) * mm});
            skLineSegment(sketch, "E122", {"start": v(4353.72, -4305.73) * mm, "end": v(-6373.4, -4305.73) * mm});
            skLineSegment(sketch, "E123", {"start": v(-6373.4, -4305.73) * mm, "end": v(-6377.03, 6179.3) * mm});
            skSolve(sketch);
        }
        {
            var Q0;
            Q0 = qSketchRegion(id + "F32", true);
            extrude(context, id + "F33", {"entities" : qUnion([Q0]), "operationType" : NewBodyOperationType.ADD, "depth" : 200 * mm, "offsetDistance" : 25 * mm});
        }
    });
